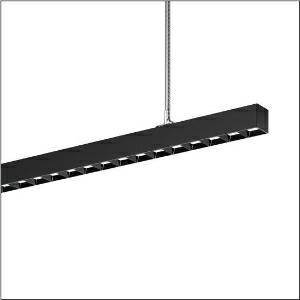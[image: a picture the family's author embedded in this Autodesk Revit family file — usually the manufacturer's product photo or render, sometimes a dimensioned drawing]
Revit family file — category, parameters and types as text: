
# Revit family: silica_21_51mx31tctdb
name_source: partatom
category: Lighting Fixtures
units: mm (PartAtom-declared; Revit-internal decimal feet)

## family parameters
Cut with Voids When Loaded = No
Host = Face
Light Source = No
Part Type = Normal
Room Calculation Point = No
Round Connector Dimension = Use Diameter
Shared = No

## types (1)
- --- (1 x LED, 15550 lm, 133.9 W, 6500K)
    Apparent Load = 134 VA
    CIE Flux Codes = 85 99 100 60 100
    Color Rendering = 80
    Color Temperature = 6500K
    Default Elevation = 1800 mm
    Description = Silica 21, office luminaire, primary light control with darklight reflector, of PMMA, black, CAT 2 (L<= 3000cd/m²), light emission: direct/indirect distribution, primary light characteristic: symmetric, installation type: suspended mounting, LED, rated luminous flux: 15.550lm, luminous efficacy: 111lm/W, light colour: 8tw, colour temperature: 2700..6500K, control gear: DALI DT8, with terminal, 3+2-pole, max. 2.5mm², mains connection: 220..240V, AC, 50/60Hz, rated input power: 140.6W, luminaire housing, of aluminium, matt jet black (RAL 9005), length: 3.004mm, width: 53mm, height: 53mm, protection rating (complete): IP20, insulation class (complete): insulation class I (protective earthing), certification: CE, permissible operating ambient temperature: 0..+35°C, standard: EN 50419, packaging unit: 1 piece
    Height = 53 mm
    Lamp = 1 x LED
    Lamp Light Flux = 15550 lm
    Lamp Power = 133.9 W
    Lamp count = 1
    Length = 3004 mm
    Luminous efficacy = 116 lm/W
    Manufacturer = Siteco
    ModVariant = No
    Model = 51MX31TCTDB
    Mounting Place = Ceiling
    Mounting Type = Pendant
    Number of Poles = 1
    OnlyDefault = Yes
    Power Factor = 1
    Product Name = Silica 21
    Product group = office luminaire | ceiling pendant
    ProductGroupID = 903
    Protection Class = Protection class I
    Protection Degree = IP 20
    RLX_Detail_Level = 1
    RLX_Emergency_Light_Flux = 0 lm
    RLX_Emergency_Type = 0
    RLX_Emergency_Type_DB = No
    RlxData = <blob elided: 63017 chars, md5=74b557f9>
    Socket = socket
    Standby Power = 0 W
    System Light Flux = 15550 lm
    System Power = 134 W
    Type Comments = individual setting
    Type Image = l_1335852.jpg
    URL = http://relux.com
    VarID = @adj_139373
    Voltage = 0 V
    Weight = 0.00 kg
    Width = 53 mm

## geometry (parser evidence)
native form markers: Blend x4, Sweep x12
no freeform markers — native parametric forms only
